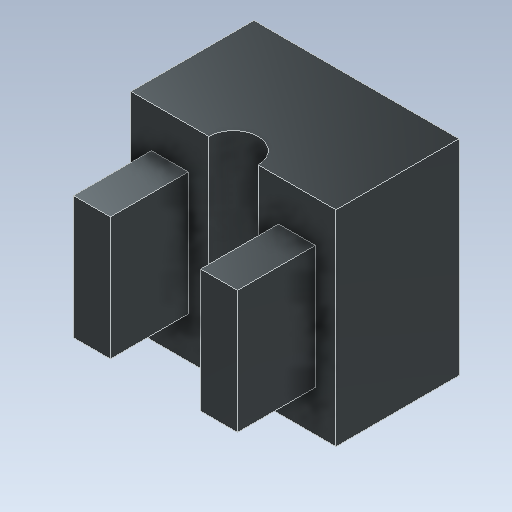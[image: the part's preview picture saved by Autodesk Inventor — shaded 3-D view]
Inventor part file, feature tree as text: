
AUTODESK INVENTOR PART (.ipt)
format: ipt  version: 2021 (Build 250183000, 183)  size: 139,264 bytes
history: native  units: in
note: dims shown in document units (in); Inventor stores cm internally (conversion verified against a paired STEP export)
features: extrude x3, sketch x3
ambient origin geometry x8: Origin, YZ Plane, XZ Plane, XY Plane, X Axis, Y Axis, Z Axis, Center Point
bodies: Solid1 (feature_tree)
feature tree (6):
  extrude  "Extrusion1"  Depth=1.9685in
  sketch  "Sketch2"  dims[d2=1.1811in d3=0.0in d4=0.3937in]
  extrude  "Extrusion2"  Depth=0.3937in
  extrude  "Extrusion3"  Depth=0.1969in
  sketch  "Sketch1"  dims[d0=1.9685in d1=1.9685in]
  sketch  "Sketch3"  dims[d5=0.3937in d6=0.1969in d7=0.1969in d8=0.4724in d9=1.9685in d10=0.0in d11=0.3543in d12=0.3543in d13=0.9843in d14=0.748in d15=0.0in]
